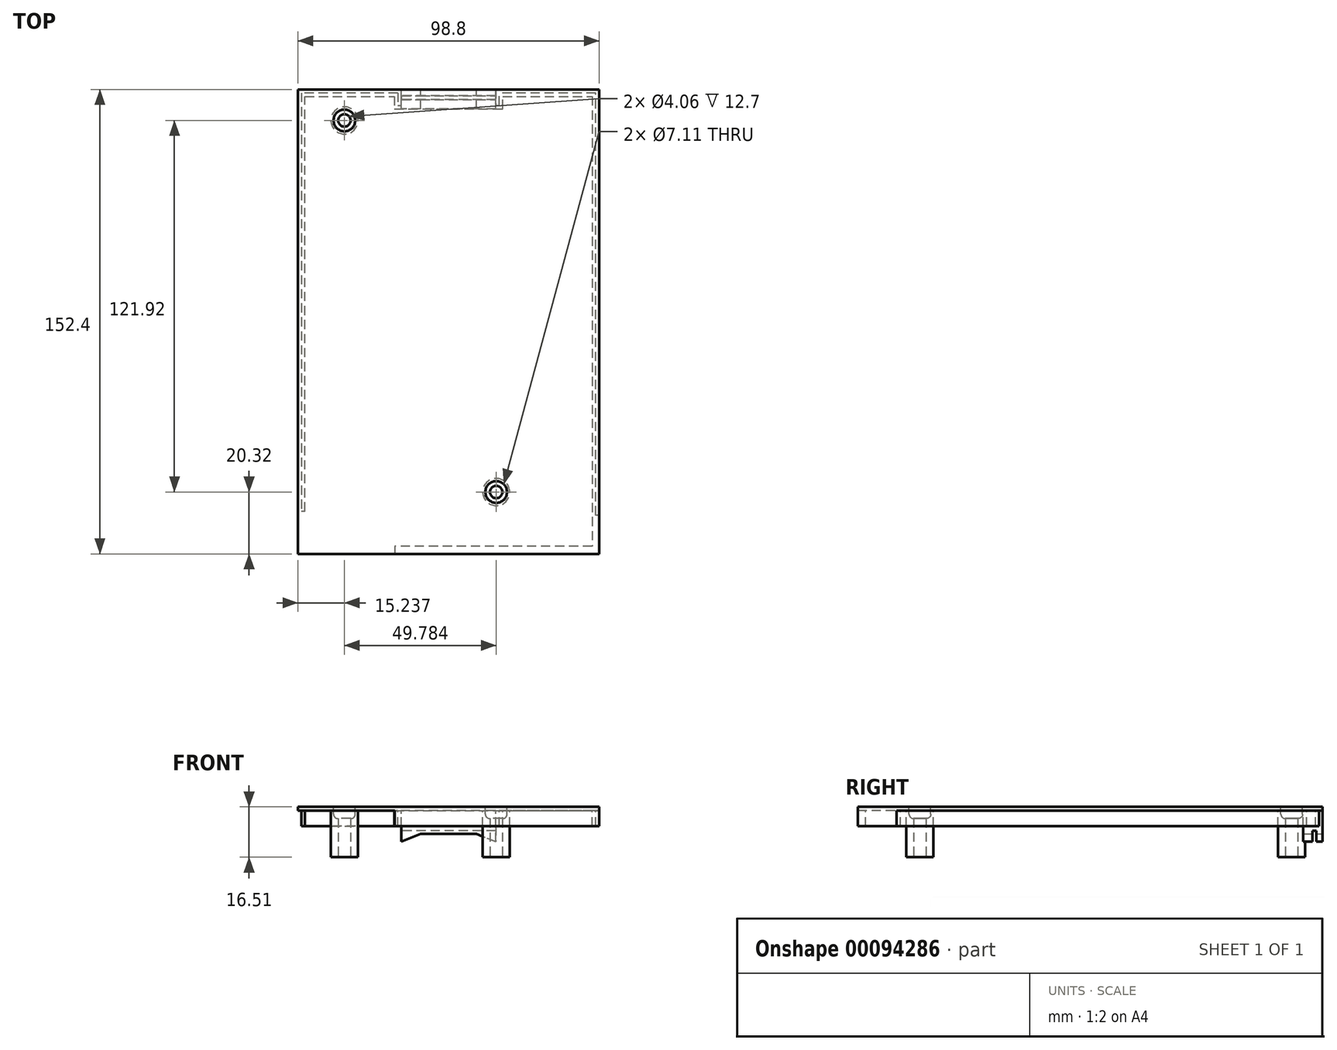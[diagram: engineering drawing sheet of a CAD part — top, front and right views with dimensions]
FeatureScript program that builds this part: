
annotation { "Feature Type Name" : "Feature", "Feature Type Description" : "" }
export const myFeature = defineFeature(function(context is Context, id is Id, definition is map)
    precondition{}
    {
        {
            var Q0;
            Q0=qCreatedBy(makeId("Top.planeOp"),FACE);
            var sketch = newSketch(context, id + "F0", { "sketchPlane" : qUnion([Q0])});
            skLineSegment(sketch, "E0.bottom", {"start": v(-49.4, 76.2) * mm, "end": v(49.4, 76.2) * mm});
            skLineSegment(sketch, "E0.top", {"start": v(-49.4, -76.2) * mm, "end": v(49.4, -76.2) * mm});
            skLineSegment(sketch, "E0.left", {"start": v(-49.4, 76.2) * mm, "end": v(-49.4, -76.2) * mm});
            skLineSegment(sketch, "E0.right", {"start": v(49.4, 76.2) * mm, "end": v(49.4, -76.2) * mm});
            skPoint(sketch, "E1", {"position": v(0, 76.2) * mm});
            skPoint(sketch, "E2", {"position": v(-49.4, 0) * mm});
            skSolve(sketch);
        }
        {
            var Q0;
            Q0 = qSketchRegion(id + "F0", true);
            extrude(context, id + "F1", {"entities" : qUnion([Q0]), "depth" : 1.27 * mm});
        }
        {
            var Q0;
            Q0=makeQuery(id+"F1.opExtrude","CAP_FACE",FACE,{"disambiguationData":[OSD([sQuery(id+"F0.wireOp",EDGE,"E0.bottom"),sQuery(id+"F0.wireOp",EDGE,"E0.top"),sQuery(id+"F0.wireOp",EDGE,"E0.left"),sQuery(id+"F0.wireOp",EDGE,"E0.right")])],"isStart":false});
            var sketch = newSketch(context, id + "F2", { "sketchPlane" : qUnion([Q0])});
            skLineSegment(sketch, "E3", {"start": v(-17.65, -76.2) * mm, "end": v(49.4, -76.2) * mm});
            skLineSegment(sketch, "E4", {"start": v(49.4, -76.2) * mm, "end": v(49.4, -63.5) * mm});
            skLineSegment(sketch, "E5", {"start": v(49.4, -63.5) * mm, "end": v(48.26, -63.5) * mm});
            skLineSegment(sketch, "E6", {"start": v(48.26, -63.5) * mm, "end": v(48.26, 75.06) * mm});
            skLineSegment(sketch, "E7", {"start": v(48.26, 75.06) * mm, "end": v(16.64, 75.06) * mm});
            skLineSegment(sketch, "E8", {"start": v(-16.64, 75.06) * mm, "end": v(-48.26, 75.06) * mm});
            skLineSegment(sketch, "E9", {"start": v(-48.26, 75.06) * mm, "end": v(-48.26, -62.23) * mm});
            skLineSegment(sketch, "E10", {"start": v(-47.12, -62.23) * mm, "end": v(-47.12, 73.91) * mm});
            skLineSegment(sketch, "E11", {"start": v(47.12, 73.91) * mm, "end": v(47.12, -73.66) * mm});
            skLineSegment(sketch, "E12", {"start": v(47.12, -73.66) * mm, "end": v(-17.65, -73.66) * mm});
            skLineSegment(sketch, "E13", {"start": v(-17.65, -73.66) * mm, "end": v(-17.65, -76.2) * mm});
            skLineSegment(sketch, "E14", {"start": v(-47.12, -62.23) * mm, "end": v(-47.12, -62.23) * mm});
            skLineSegment(sketch, "E15", {"start": v(-47.12, 73.91) * mm, "end": v(-47.12, 75.06) * mm, "construction": true});
            skLineSegment(sketch, "E16", {"start": v(-48.26, 75.06) * mm, "end": v(-49.4, 75.06) * mm, "construction": true});
            skLineSegment(sketch, "E17", {"start": v(47.12, 73.91) * mm, "end": v(48.26, 73.91) * mm, "construction": true});
            skLineSegment(sketch, "E18", {"start": v(-47.12, -62.23) * mm, "end": v(-48.26, -62.23) * mm});
            skLineSegment(sketch, "E19", {"start": v(-48.26, 75.06) * mm, "end": v(-48.26, 76.2) * mm, "construction": true});
            skLineSegment(sketch, "E20", {"start": v(-16.64, 75.06) * mm, "end": v(-16.64, 71) * mm});
            skLineSegment(sketch, "E21", {"start": v(-16.64, 71) * mm, "end": v(-15.5, 71) * mm});
            skLineSegment(sketch, "E22", {"start": v(-15.5, 71) * mm, "end": v(-15.5, 76.2) * mm});
            skLineSegment(sketch, "E23", {"start": v(-15.5, 76.2) * mm, "end": v(15.5, 76.2) * mm});
            skLineSegment(sketch, "E24", {"start": v(15.5, 76.2) * mm, "end": v(15.5, 71) * mm});
            skLineSegment(sketch, "E25", {"start": v(15.5, 71) * mm, "end": v(16.64, 71) * mm});
            skLineSegment(sketch, "E26", {"start": v(16.64, 71) * mm, "end": v(16.64, 75.06) * mm});
            skLineSegment(sketch, "E27", {"start": v(-47.12, 73.91) * mm, "end": v(-17.78, 73.91) * mm});
            skLineSegment(sketch, "E28", {"start": v(-17.78, 73.91) * mm, "end": v(-17.78, 69.85) * mm});
            skLineSegment(sketch, "E29", {"start": v(-17.78, 69.85) * mm, "end": v(17.78, 69.85) * mm});
            skLineSegment(sketch, "E30", {"start": v(17.78, 69.85) * mm, "end": v(17.78, 73.91) * mm});
            skLineSegment(sketch, "E31", {"start": v(17.78, 73.91) * mm, "end": v(47.12, 73.91) * mm});
            skPoint(sketch, "E32", {"position": v(0, 76.2) * mm});
            skLineSegment(sketch, "E33", {"start": v(-16.64, 71) * mm, "end": v(-17.78, 71) * mm, "construction": true});
            skLineSegment(sketch, "E34", {"start": v(16.64, 71) * mm, "end": v(17.78, 71) * mm, "construction": true});
            skLineSegment(sketch, "E35", {"start": v(-15.5, 71) * mm, "end": v(-15.5, 69.85) * mm, "construction": true});
            skSolve(sketch);
        }
        {
            var Q0;
            Q0 = qSketchRegion(id + "F2", true);
            extrude(context, id + "F3", {"entities" : qUnion([Q0]), "operationType" : NewBodyOperationType.ADD, "oppositeDirection" : true, "depth" : 6.35 * mm});
        }
        {
            var Q0;
            {var subQ0=sQuery(id+"F0.wireOp",EDGE,"E0.bottom");var subQ1=sQuery(id+"F0.wireOp",EDGE,"E0.top");var subQ2=sQuery(id+"F0.wireOp",EDGE,"E0.left");Q0=makeQuery(id+"F3.boolean.opBoolean","SPLIT",FACE,{"disambiguationData":[TD([makeQuery(id+"F1.opExtrude","SWEPT_FACE",FACE,{"disambiguationData":[OSD([subQ1])]})])],"derivedFrom":makeQuery(id+"F1.opExtrude","CAP_FACE",FACE,{"disambiguationData":[OSD([subQ0,subQ1,subQ2,sQuery(id+"F0.wireOp",EDGE,"E0.right")])],"isStart":true})});}
            var sketch = newSketch(context, id + "F4", { "sketchPlane" : qUnion([Q0])});
            skCircle(sketch, "E36", {"center": v(15.62, 55.88) * mm, "radius": 4.45 * mm});
            skCircle(sketch, "E37", {"center": v(-34.16, -66.04) * mm, "radius": 4.45 * mm});
            skSolve(sketch);
        }
        {
            var Q0;
            Q0 = qSketchRegion(id + "F4", true);
            extrude(context, id + "F5", {"entities" : qUnion([Q0]), "operationType" : NewBodyOperationType.ADD, "depth" : 15.24 * mm});
        }
        {
            var Q0;
            Q0=makeQuery(id+"F5.opExtrude","CAP_FACE",FACE,{"disambiguationData":[OSD([sQuery(id+"F4.wireOp",EDGE,"E37")])],"isStart":false});
            var sketch = newSketch(context, id + "F6", { "sketchPlane" : qUnion([Q0])});
            skCircle(sketch, "E38", {"center": v(-34.16, -66.04) * mm, "radius": 2.03 * mm});
            skCircle(sketch, "E39", {"center": v(15.62, 55.88) * mm, "radius": 2.03 * mm});
            skSolve(sketch);
        }
        {
            var Q0;
            Q0 = qSketchRegion(id + "F6", true);
            var Q1;
            Q1=makeQuery(id+"F1.opExtrude","CAP_FACE",FACE,{"disambiguationData":[OSD([sQuery(id+"F0.wireOp",EDGE,"E0.bottom"),sQuery(id+"F0.wireOp",EDGE,"E0.top"),sQuery(id+"F0.wireOp",EDGE,"E0.left"),sQuery(id+"F0.wireOp",EDGE,"E0.right")])],"isStart":false});
            extrude(context, id + "F7", {"entities" : qUnion([Q0]), "operationType" : NewBodyOperationType.REMOVE, "endBound" : BoundingType.UP_TO_SURFACE, "oppositeDirection" : true, "endBoundEntityFace" : qUnion([Q1]), "depth" : 25.4 * mm});
        }
        {
            var Q0;
            Q0=makeQuery(id+"F1.opExtrude","CAP_FACE",FACE,{"disambiguationData":[OSD([sQuery(id+"F0.wireOp",EDGE,"E0.bottom"),sQuery(id+"F0.wireOp",EDGE,"E0.top"),sQuery(id+"F0.wireOp",EDGE,"E0.left"),sQuery(id+"F0.wireOp",EDGE,"E0.right")])],"isStart":false});
            var sketch = newSketch(context, id + "F8", { "sketchPlane" : qUnion([Q0])});
            skCircle(sketch, "E40", {"center": v(15.62, -55.88) * mm, "radius": 3.56 * mm});
            skCircle(sketch, "E41", {"center": v(-34.16, 66.04) * mm, "radius": 3.56 * mm});
            skSolve(sketch);
        }
        {
            var Q0;
            Q0 = qSketchRegion(id + "F8", true);
            extrude(context, id + "F9", {"entities" : qUnion([Q0]), "operationType" : NewBodyOperationType.REMOVE, "oppositeDirection" : true, "depth" : 3.8 * mm});
        }
        {
            var Q0;
            Q0=makeQuery(id+"F3.boolean.opBoolean","MERGE",FACE,{"derivedFrom":[makeQuery(id+"F1.opExtrude","SWEPT_FACE",FACE,{"disambiguationData":[OSD([sQuery(id+"F0.wireOp",EDGE,"E0.bottom")])]}),makeQuery(id+"F3.opExtrude","SWEPT_FACE",FACE,{"disambiguationData":[OSD([sQuery(id+"F2.wireOp",EDGE,"E23")])]})]});
            var sketch = newSketch(context, id + "F10", { "sketchPlane" : qUnion([Q0])});
            skLineSegment(sketch, "E42", {"start": v(-15.5, -5.08) * mm, "end": v(-15.5, -10.16) * mm});
            skLineSegment(sketch, "E43", {"start": v(-15.5, -10.16) * mm, "end": v(-9.14, -7.62) * mm});
            skLineSegment(sketch, "E44", {"start": v(-9.14, -7.62) * mm, "end": v(9.14, -7.62) * mm});
            skLineSegment(sketch, "E45", {"start": v(9.14, -7.62) * mm, "end": v(15.5, -10.16) * mm});
            skLineSegment(sketch, "E46", {"start": v(15.5, -10.16) * mm, "end": v(15.5, -5.08) * mm});
            skLineSegment(sketch, "E47", {"start": v(15.5, -5.08) * mm, "end": v(-15.5, -5.08) * mm});
            skPoint(sketch, "E48", {"position": v(0, -7.62) * mm});
            skSolve(sketch);
        }
        {
            var Q0;
            Q0 = qSketchRegion(id + "F10", true);
            var Q1;
            Q1=makeQuery(id+"F3.opExtrude","SWEPT_FACE",FACE,{"disambiguationData":[OSD([sQuery(id+"F2.wireOp",EDGE,"E29")])]});
            extrude(context, id + "F11", {"entities" : qUnion([Q0]), "operationType" : NewBodyOperationType.ADD, "endBound" : BoundingType.UP_TO_SURFACE, "oppositeDirection" : true, "endBoundEntityFace" : qUnion([Q1]), "depth" : 25.4 * mm});
        }
        {
            var Q0;
            Q0=makeQuery(id+"F11.boolean.opBoolean","MERGE",FACE,{"derivedFrom":[makeQuery(id+"F3.opExtrude","SWEPT_FACE",FACE,{"disambiguationData":[OSD([sQuery(id+"F2.wireOp",EDGE,"E22")])]}),makeQuery(id+"F11.opExtrude","SWEPT_FACE",FACE,{"disambiguationData":[OSD([sQuery(id+"F10.wireOp",EDGE,"E46")])]})]});
            var sketch = newSketch(context, id + "F12", { "sketchPlane" : qUnion([Q0])});
            skLineSegment(sketch, "E49.bottom", {"start": v(-74.17, -6.6) * mm, "end": v(-72.9, -6.6) * mm});
            skLineSegment(sketch, "E49.top", {"start": v(-74.17, -10.16) * mm, "end": v(-72.9, -10.16) * mm});
            skLineSegment(sketch, "E49.left", {"start": v(-74.17, -6.6) * mm, "end": v(-74.17, -10.16) * mm});
            skLineSegment(sketch, "E49.right", {"start": v(-72.9, -6.6) * mm, "end": v(-72.9, -10.16) * mm});
            skLineSegment(sketch, "E50", {"start": v(-74.17, -7.62) * mm, "end": v(-72.9, -7.62) * mm, "construction": true});
            skSolve(sketch);
        }
        {
            var Q0;
            Q0 = qSketchRegion(id + "F12", true);
            var Q1;
            Q1=makeQuery(id+"F11.boolean.opBoolean","MERGE",FACE,{"derivedFrom":[makeQuery(id+"F3.opExtrude","SWEPT_FACE",FACE,{"disambiguationData":[OSD([sQuery(id+"F2.wireOp",EDGE,"E24")])]}),makeQuery(id+"F11.opExtrude","SWEPT_FACE",FACE,{"disambiguationData":[OSD([sQuery(id+"F10.wireOp",EDGE,"E42")])]})]});
            extrude(context, id + "F13", {"entities" : qUnion([Q0]), "operationType" : NewBodyOperationType.REMOVE, "endBound" : BoundingType.UP_TO_SURFACE, "oppositeDirection" : true, "endBoundEntityFace" : qUnion([Q1]), "depth" : 25.4 * mm});
        }
        {
            var Q0;
            Q0=makeQuery(id+"F9.boolean.opBoolean","COPY",EDGE,{"derivedFrom":makeQuery(id+"F9.opExtrude","CAP_EDGE",EDGE,{"disambiguationData":[OSD([sQuery(id+"F8.wireOp",EDGE,"E40")])],"isStart":false})});
            var Q1;
            Q1=makeQuery(id+"F9.boolean.opBoolean","COPY",EDGE,{"derivedFrom":makeQuery(id+"F9.opExtrude","CAP_EDGE",EDGE,{"disambiguationData":[OSD([sQuery(id+"F8.wireOp",EDGE,"E41")])],"isStart":false})});
            fillet(context, id + "F14", {"entities" : qUnion([Q0, Q1]), "radius" : 1.4 * mm, "tangentPropagation" : true, "allowEdgeOverflow" : false});
        }
    });
